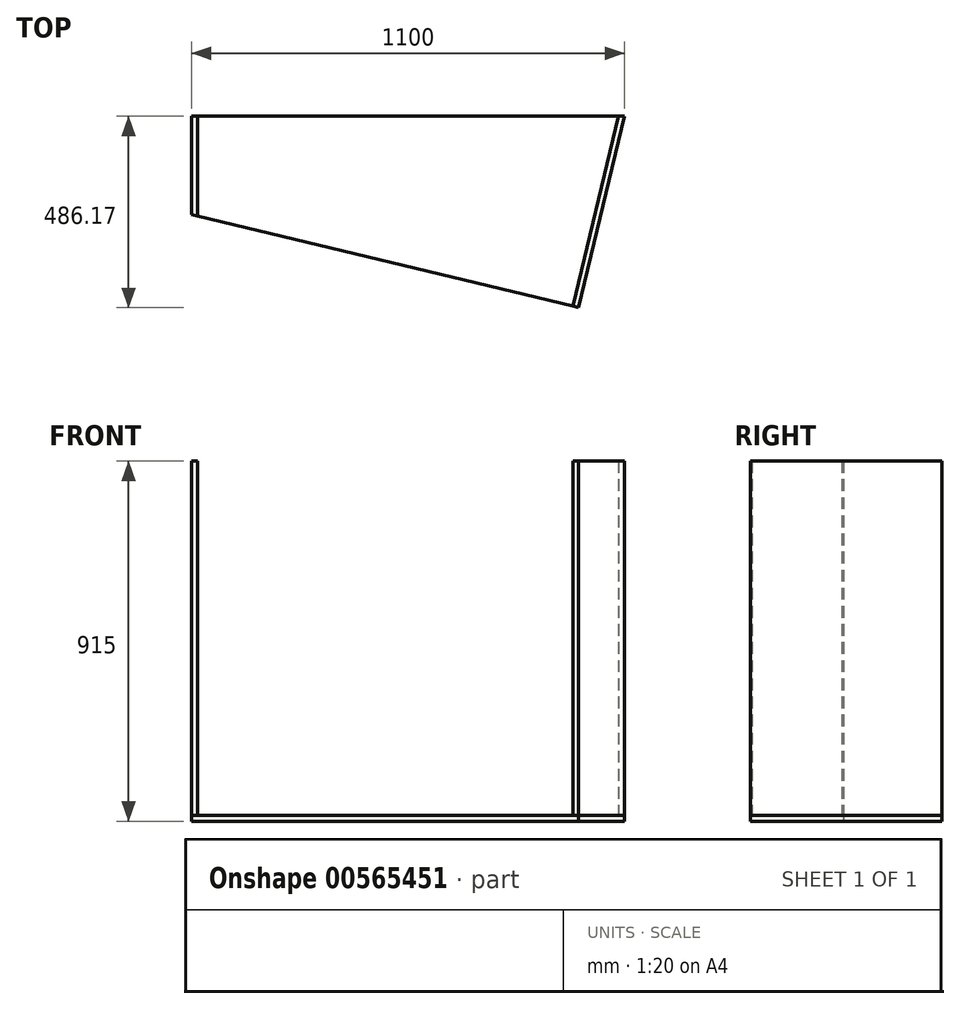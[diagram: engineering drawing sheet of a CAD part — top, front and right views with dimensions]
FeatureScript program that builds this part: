
annotation { "Feature Type Name" : "Feature", "Feature Type Description" : "" }
export const myFeature = defineFeature(function(context is Context, id is Id, definition is map)
    precondition{}
    {
        {
            var Q0;
            Q0=qCreatedBy(makeId("Top.planeOp"),FACE);
            var sketch = newSketch(context, id + "F0", { "sketchPlane" : qUnion([Q0])});
            skLineSegment(sketch, "E0", {"start": v(-550, 0) * mm, "end": v(-550, -250) * mm});
            skLineSegment(sketch, "E1", {"start": v(-550, -250) * mm, "end": v(433.22, -486.17) * mm});
            skLineSegment(sketch, "E2", {"start": v(433.22, -486.17) * mm, "end": v(550, 0) * mm});
            skLineSegment(sketch, "E3", {"start": v(550, 0) * mm, "end": v(-550, 0) * mm});
            skSolve(sketch);
        }
        {
            var Q0;
            Q0=makeQuery(id+"F0.imprint","IMPRINT",FACE,{"disambiguationData":[TD([[makeQuery(id+"F0.imprint","IMPRINT",EDGE,{"derivedFrom":sQuery(id+"F0.wireOp",EDGE,"E0")}),1.0]])]});
            extrude(context, id + "F1", {"entities" : qUnion([Q0]), "depth" : 15 * mm, "offsetDistance" : 25 * mm});
        }
        {
            var Q0;
            Q0=makeQuery(id+"F1.opExtrude","CAP_FACE",FACE,{"disambiguationData":[OSD([sQuery(id+"F0.wireOp",EDGE,"E0"),sQuery(id+"F0.wireOp",EDGE,"E1"),sQuery(id+"F0.wireOp",EDGE,"E2"),sQuery(id+"F0.wireOp",EDGE,"E3")])],"isStart":false});
            var sketch = newSketch(context, id + "F2", { "sketchPlane" : qUnion([Q0])});
            skLineSegment(sketch, "E4", {"start": v(-550, 0) * mm, "end": v(-550, -250) * mm});
            skLineSegment(sketch, "E5", {"start": v(-550, -250) * mm, "end": v(-535, -253.6) * mm});
            skLineSegment(sketch, "E6", {"start": v(-535, -253.6) * mm, "end": v(-535, 0) * mm});
            skLineSegment(sketch, "E7", {"start": v(-535, 0) * mm, "end": v(-550, 0) * mm});
            skLineSegment(sketch, "E8", {"start": v(550, 0) * mm, "end": v(433.22, -486.17) * mm});
            skLineSegment(sketch, "E9", {"start": v(433.22, -486.17) * mm, "end": v(418.64, -482.67) * mm});
            skLineSegment(sketch, "E10", {"start": v(418.64, -482.67) * mm, "end": v(534.57, 0) * mm});
            skLineSegment(sketch, "E11", {"start": v(534.57, 0) * mm, "end": v(550, 0) * mm});
            skSolve(sketch);
        }
        {
            var Q0;
            Q0 = qSketchRegion(id + "F2", true);
            extrude(context, id + "F3", {"entities" : qUnion([Q0]), "depth" : 900 * mm, "offsetDistance" : 25 * mm});
        }
    });
